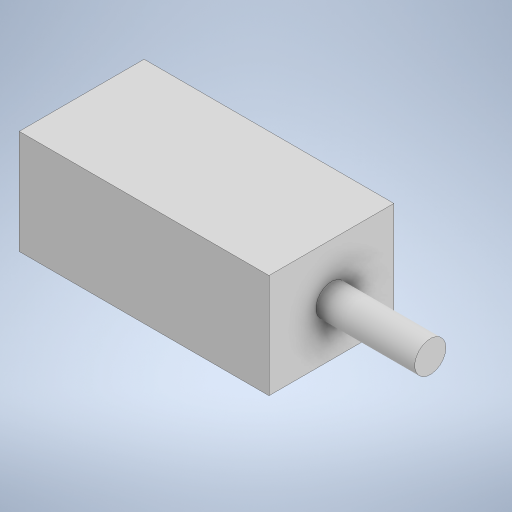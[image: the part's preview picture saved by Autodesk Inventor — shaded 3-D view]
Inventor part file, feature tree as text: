
AUTODESK INVENTOR PART (.ipt)
format: ipt  version: 2024 (Build 280153020, 153B)  size: 212,992 bytes
history: native  units: mm
features: extrude x2, sketch x2
ambient origin geometry x8: Origin, YZ Plane, XZ Plane, XY Plane, X Axis, Y Axis, Z Axis, Center Point
bodies: Solid1 (feature_tree)
feature tree (4):
  extrude  "Extrusion1"  Depth=12.0mm
  extrude  "Extrusion2"  Depth=9.5mm
  sketch  "Sketch1"  dims[d0=24.0mm d1=12.0mm]
  sketch  "Sketch2"  dims[d2=10.0mm d3=0.0mm d4=3.0mm d5=9.5mm d6=0.0mm]
